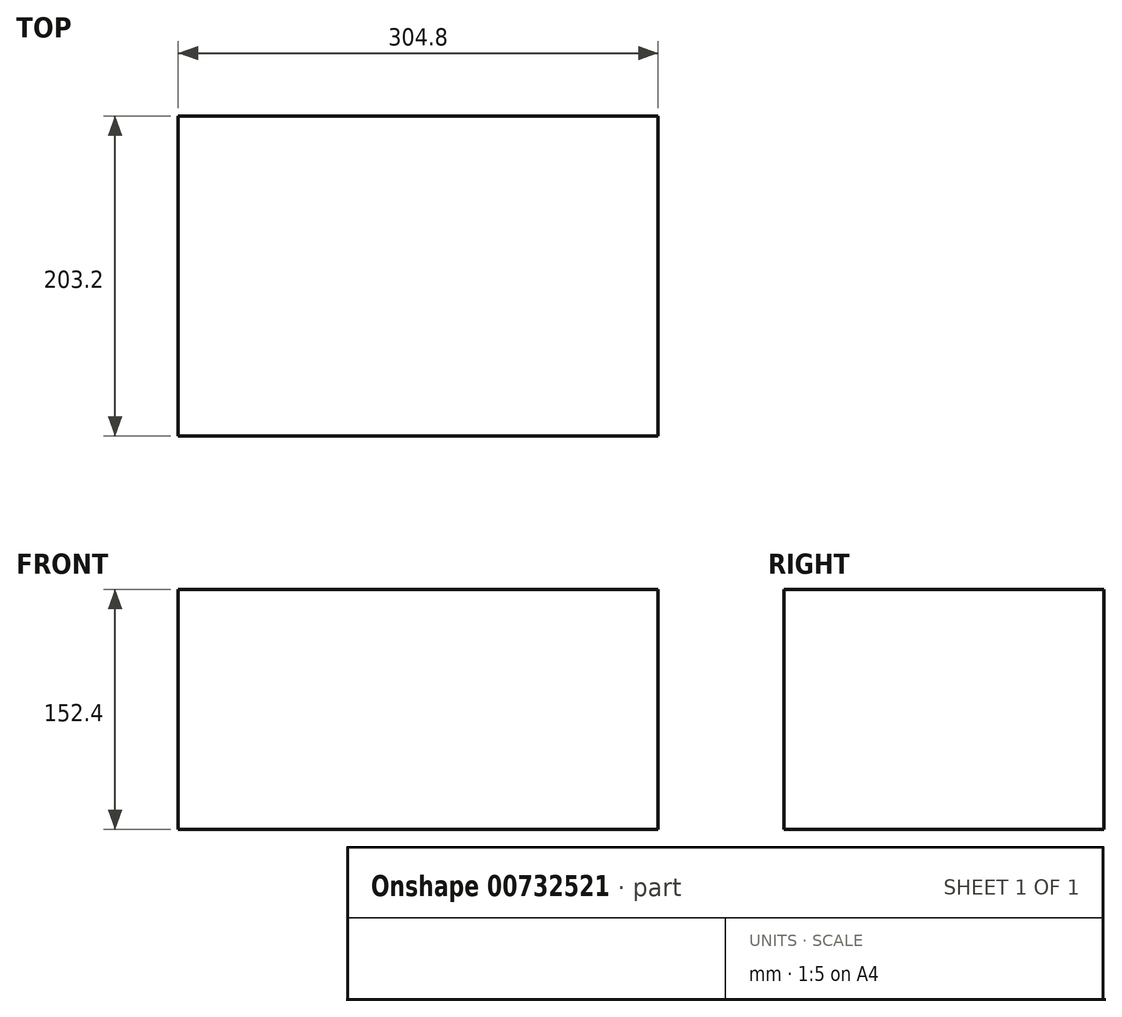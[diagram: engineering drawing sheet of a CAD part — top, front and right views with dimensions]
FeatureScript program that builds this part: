
annotation { "Feature Type Name" : "Feature", "Feature Type Description" : "" }
export const myFeature = defineFeature(function(context is Context, id is Id, definition is map)
    precondition{}
    {
        {
            var Q0;
            Q0=qCreatedBy(makeId("Front.planeOp"),FACE);
            var sketch = newSketch(context, id + "F0", { "sketchPlane" : qUnion([Q0])});
            skLineSegment(sketch, "E0.bottom", {"start": v(-152.4, 0) * mm, "end": v(152.4, 0) * mm});
            skLineSegment(sketch, "E0.top", {"start": v(-152.4, 152.4) * mm, "end": v(152.4, 152.4) * mm});
            skLineSegment(sketch, "E0.left", {"start": v(-152.4, 0) * mm, "end": v(-152.4, 152.4) * mm});
            skLineSegment(sketch, "E0.right", {"start": v(152.4, 0) * mm, "end": v(152.4, 152.4) * mm});
            skSolve(sketch);
        }
        {
            var Q0;
            Q0=makeQuery(id+"F0.imprint","IMPRINT",FACE,{"disambiguationData":[TD([[makeQuery(id+"F0.imprint","IMPRINT",EDGE,{"derivedFrom":sQuery(id+"F0.wireOp",EDGE,"E0.bottom")}),1.0]])]});
            extrude(context, id + "F1", {"entities" : qUnion([Q0]), "oppositeDirection" : true, "depth" : 203.2 * mm, "offsetDistance" : 25.4 * mm});
        }
        {
            var Q0;
            Q0=qCreatedBy(makeId("Front.planeOp"),FACE);
            cPlane(context, id + "F2", {"entities" : qUnion([Q0]), "cplaneType" : CPlaneType.OFFSET, "offset" : 101.6 * mm, "oppositeDirection" : true, "width" : 152.4 * mm, "height" : 152.4 * mm});
        }
        {
            var Q0;
            Q0=qCreatedBy(id+"F2.planeOp",FACE);
            var sketch = newSketch(context, id + "F3", { "sketchPlane" : qUnion([Q0])});
            skCircle(sketch, "E1", {"center": v(330.2, 0) * mm, "radius": 36.2 * mm});
            skLineSegment(sketch, "E2", {"start": v(330.2, 0) * mm, "end": v(362.06, -17.17) * mm});
            skLineSegment(sketch, "E3", {"start": v(362.06, -17.17) * mm, "end": v(233.45, 52.05) * mm});
            skLineSegment(sketch, "E4", {"start": v(233.45, 52.05) * mm, "end": v(177.8, 0) * mm});
            skLineSegment(sketch, "E5", {"start": v(330.2, 0) * mm, "end": v(-287.02, 0) * mm, "construction": true});
            skCircle(sketch, "E6.MirrorC", {"center": v(-330.2, 0) * mm, "radius": 36.2 * mm});
            skLineSegment(sketch, "E7.MirrorCS", {"start": v(-330.2, 0) * mm, "end": v(-362.37, -16.6) * mm});
            skLineSegment(sketch, "E8.MirrorCS", {"start": v(-233.45, 52.05) * mm, "end": v(-177.8, 0) * mm});
            skLineSegment(sketch, "E9.MirrorCS", {"start": v(-362.37, -16.6) * mm, "end": v(-233.45, 52.05) * mm});
            skSolve(sketch);
        }
        {
            var Q0;
            Q0=qCreatedBy(makeId("Right.planeOp"),FACE);
            var sketch = newSketch(context, id + "F4", { "sketchPlane" : qUnion([Q0])});
            skLineSegment(sketch, "E10", {"start": v(-64.38, 152.4) * mm, "end": v(271.63, 152.4) * mm, "construction": true});
            skLineSegment(sketch, "E11", {"start": v(-170.54, 241.3) * mm, "end": v(292.68, 241.3) * mm, "construction": true});
            skCircle(sketch, "E12", {"center": v(-101.6, 241.3) * mm, "radius": 44.45 * mm});
            skCircle(sketch, "E13", {"center": v(304.8, 241.3) * mm, "radius": 44.45 * mm});
            skLineSegment(sketch, "E14", {"start": v(-101.6, 241.3) * mm, "end": v(-130.68, 274.91) * mm});
            skLineSegment(sketch, "E15", {"start": v(-130.68, 274.91) * mm, "end": v(-40.04, 152.4) * mm});
            skLineSegment(sketch, "E16", {"start": v(304.8, 241.3) * mm, "end": v(334.97, 273.95) * mm});
            skLineSegment(sketch, "E17", {"start": v(334.97, 273.95) * mm, "end": v(243.03, 152.4) * mm});
            skLineSegment(sketch, "E18.0.0", {"start": v(0, 152.4) * mm, "end": v(0, 0) * mm});
            skLineSegment(sketch, "E18.0.1", {"start": v(0, 0) * mm, "end": v(203.2, 0) * mm});
            skLineSegment(sketch, "E18.0.2", {"start": v(203.2, 0) * mm, "end": v(203.2, 152.4) * mm});
            skLineSegment(sketch, "E18.0.3", {"start": v(203.2, 152.4) * mm, "end": v(0, 152.4) * mm});
            skPoint(sketch, "E19.startSnap0", {"position": v(0, 76.2) * mm});
            skLineSegment(sketch, "E20", {"start": v(-366.48, 76.2) * mm, "end": v(539.75, 76.2) * mm, "construction": true});
            skPoint(sketch, "E21.startSnap0", {"position": v(103.63, 152.4) * mm});
            skSolve(sketch);
        }
        {
            var Q0;
            Q0=qCreatedBy(makeId("Front.planeOp"),FACE);
            cPlane(context, id + "F5", {"entities" : qUnion([Q0]), "cplaneType" : CPlaneType.OFFSET, "offset" : 25.4 * mm, "width" : 152.4 * mm, "height" : 152.4 * mm});
        }
    });
